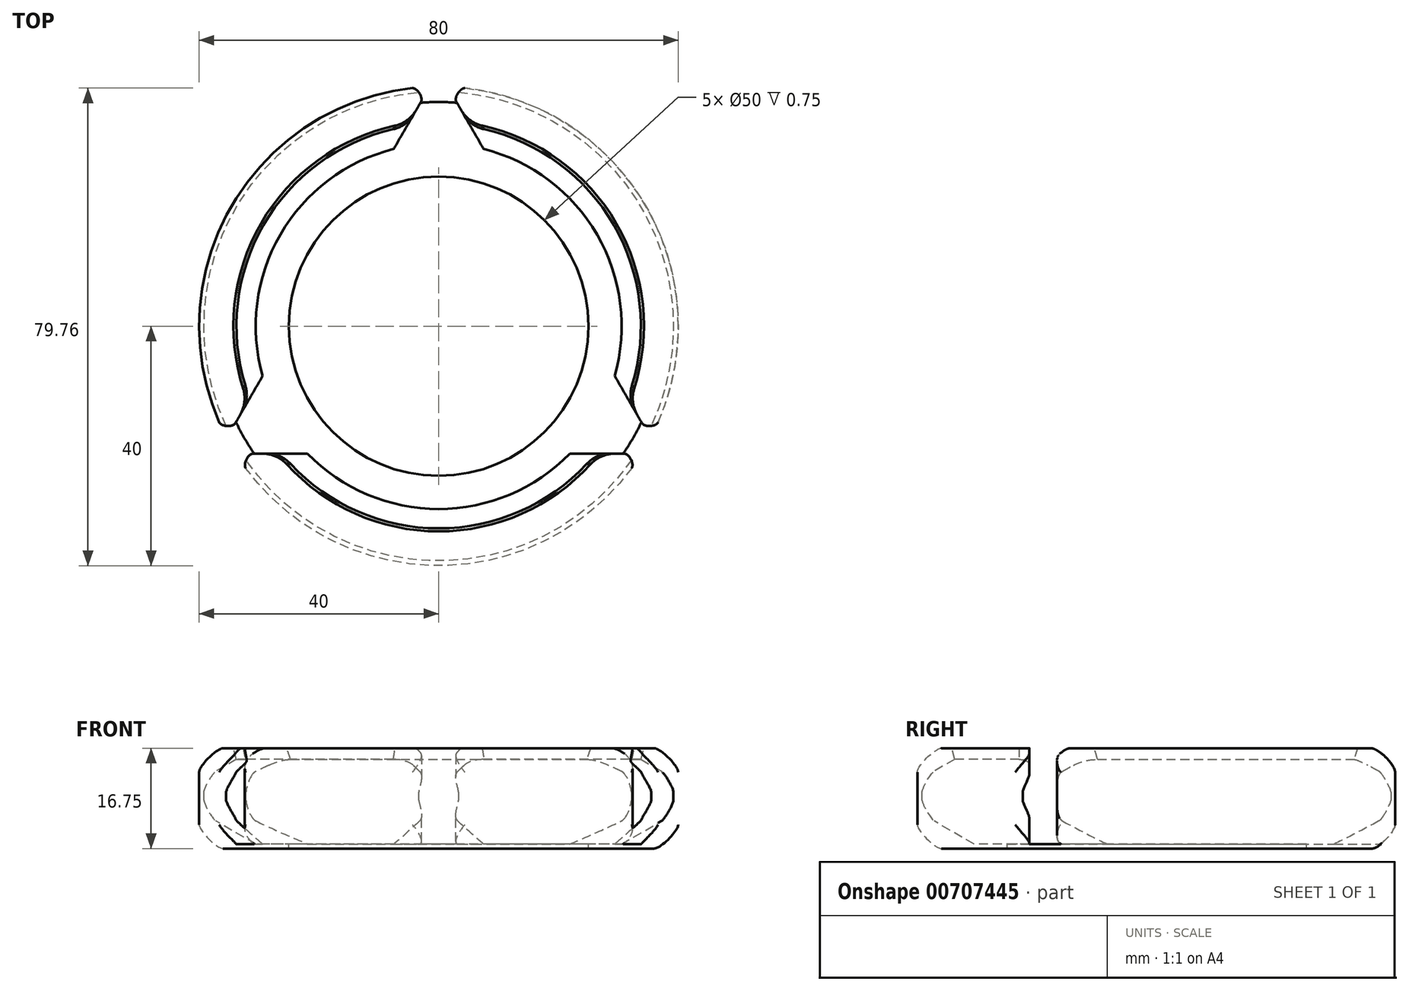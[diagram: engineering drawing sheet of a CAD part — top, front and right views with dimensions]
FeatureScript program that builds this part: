
annotation { "Feature Type Name" : "Feature", "Feature Type Description" : "" }
export const myFeature = defineFeature(function(context is Context, id is Id, definition is map)
    precondition{}
    {
        {
            var Q0;
            Q0=qCreatedBy(makeId("Right.planeOp"),FACE);
            var sketch = newSketch(context, id + "F0", { "sketchPlane" : qUnion([Q0])});
            skLineSegment(sketch, "E0", {"start": v(0, 0) * mm, "end": v(40, 0) * mm});
            skLineSegment(sketch, "E1", {"start": v(40, 0) * mm, "end": v(40, 16.75) * mm});
            skLineSegment(sketch, "E2", {"start": v(40, 16.75) * mm, "end": v(30.54, 16.75) * mm});
            skLineSegment(sketch, "E3", {"start": v(30.54, 16.75) * mm, "end": v(39.2, 11.75) * mm});
            skLineSegment(sketch, "E4", {"start": v(39.2, 11.75) * mm, "end": v(39.2, 5.75) * mm});
            skLineSegment(sketch, "E5", {"start": v(39.2, 5.75) * mm, "end": v(30.54, 0.75) * mm});
            skLineSegment(sketch, "E6", {"start": v(30.54, 0.75) * mm, "end": v(0, 0.75) * mm});
            skLineSegment(sketch, "E7", {"start": v(0, 0.75) * mm, "end": v(0, 0) * mm});
            skLineSegment(sketch, "E8", {"start": v(30.54, 0.75) * mm, "end": v(30.54, 16.75) * mm, "construction": true});
            skSolve(sketch);
        }
        {
            var Q0;
            Q0 = qSketchRegion(id + "F0", true);
            var Q1;
            Q1=sQuery(id+"F0.wireOp",EDGE,"E7");
            revolve(context, id + "F1", {"surfaceOperationType" : NewSurfaceOperationType.NEW, "entities" : qUnion([Q0]), "axis" : qUnion([Q1]), "revolveType" : RevolveType.FULL});
        }
        {
            var Q0;
            Q0=makeQuery(id+"F1.opRevolve","SWEPT_EDGE",EDGE,{"disambiguationData":[OSD([sQuery(id+"F0.wireOp",EDGE,"E0"),sQuery(id+"F0.wireOp",EDGE,"E1")])]});
            var Q1;
            Q1=makeQuery(id+"F1.opRevolve","SWEPT_EDGE",EDGE,{"disambiguationData":[OSD([sQuery(id+"F0.wireOp",EDGE,"E1"),sQuery(id+"F0.wireOp",EDGE,"E2")])]});
            var Q2;
            Q2=makeQuery(id+"F1.opRevolve","SWEPT_EDGE",EDGE,{"disambiguationData":[OSD([sQuery(id+"F0.wireOp",EDGE,"E4"),sQuery(id+"F0.wireOp",EDGE,"E5")])]});
            var Q3;
            Q3=makeQuery(id+"F1.opRevolve","SWEPT_FACE",FACE,{"disambiguationData":[OSD([sQuery(id+"F0.wireOp",EDGE,"E4")])]});
            fillet(context, id + "F2", {"entities" : qUnion([Q0, Q1, Q2, Q3]), "radius" : 4 * mm, "tangentPropagation" : true, "rho" : .2, "crossSection" : FilletCrossSection.CONIC, "allowEdgeOverflow" : false});
        }
        {
            var Q0;
            Q0=makeQuery(id+"F1.opRevolve","SWEPT_EDGE",EDGE,{"disambiguationData":[OSD([sQuery(id+"F0.wireOp",EDGE,"E2"),sQuery(id+"F0.wireOp",EDGE,"E3")])]});
            chamfer(context, id + "F3", {"entities" : qUnion([Q0]), "width" : 1 * mm, "tangentPropagation" : true});
        }
        {
            var Q0;
            Q0=makeQuery(id+"F1.opRevolve","SWEPT_FACE",FACE,{"disambiguationData":[OSD([sQuery(id+"F0.wireOp",EDGE,"E2")])]});
            var sketch = newSketch(context, id + "F4", { "sketchPlane" : qUnion([Q0])});
            skLineSegment(sketch, "E9", {"start": v(-1.5, 40) * mm, "end": v(1.5, 40) * mm});
            skLineSegment(sketch, "E10", {"start": v(1.5, 40) * mm, "end": v(35.4, -18.7) * mm});
            skLineSegment(sketch, "E11", {"start": v(35.4, -18.7) * mm, "end": v(33.9, -21.3) * mm});
            skLineSegment(sketch, "E12", {"start": v(33.9, -21.3) * mm, "end": v(-33.9, -21.3) * mm});
            skLineSegment(sketch, "E13", {"start": v(-33.9, -21.3) * mm, "end": v(-35.4, -18.7) * mm});
            skLineSegment(sketch, "E14", {"start": v(-35.4, -18.7) * mm, "end": v(-1.5, 40) * mm});
            skLineSegment(sketch, "E15", {"start": v(0, 40) * mm, "end": v(0, 0) * mm, "construction": true});
            skLineSegment(sketch, "E16", {"start": v(0, 0) * mm, "end": v(34.64, -20) * mm, "construction": true});
            skLineSegment(sketch, "E17", {"start": v(-34.64, -20) * mm, "end": v(0, 0) * mm, "construction": true});
            skSolve(sketch);
        }
        {
            var Q0;
            Q0 = qSketchRegion(id + "F4", true);
            var Q1;
            Q1=makeQuery(id+"F1.opRevolve","SWEPT_FACE",FACE,{"disambiguationData":[OSD([sQuery(id+"F0.wireOp",EDGE,"E6")])]});
            extrude(context, id + "F5", {"entities" : qUnion([Q0]), "operationType" : NewBodyOperationType.REMOVE, "endBound" : BoundingType.UP_TO_SURFACE, "oppositeDirection" : true, "depth" : 25 * mm, "endBoundEntityFace" : qUnion([Q1]), "offsetDistance" : 25 * mm});
        }
        {
            var Q0;
            Q0=makeQuery(id+"F5.boolean.opBoolean","INTERSECT",EDGE,{"disambiguationData":[OD(0.0)],"derivedFrom":[makeQuery(id+"F1.opRevolve","SWEPT_FACE",FACE,{"disambiguationData":[OSD([sQuery(id+"F0.wireOp",EDGE,"E1")])]}),makeQuery(id+"F5.opExtrude","SWEPT_FACE",FACE,{"disambiguationData":[OSD([sQuery(id+"F4.wireOp",EDGE,"E14")])]})]});
            var Q1;
            Q1=makeQuery(id+"F5.boolean.opBoolean","INTERSECT",EDGE,{"disambiguationData":[OD(0.0)],"derivedFrom":[makeQuery(id+"F1.opRevolve","SWEPT_FACE",FACE,{"disambiguationData":[OSD([sQuery(id+"F0.wireOp",EDGE,"E1")])]}),makeQuery(id+"F5.opExtrude","SWEPT_FACE",FACE,{"disambiguationData":[OSD([sQuery(id+"F4.wireOp",EDGE,"E12")])]})]});
            var Q2;
            Q2=makeQuery(id+"F5.boolean.opBoolean","INTERSECT",EDGE,{"disambiguationData":[OD(1.0)],"derivedFrom":[makeQuery(id+"F1.opRevolve","SWEPT_FACE",FACE,{"disambiguationData":[OSD([sQuery(id+"F0.wireOp",EDGE,"E1")])]}),makeQuery(id+"F5.opExtrude","SWEPT_FACE",FACE,{"disambiguationData":[OSD([sQuery(id+"F4.wireOp",EDGE,"E10")])]})]});
            var Q3;
            Q3=makeQuery(id+"F5.boolean.opBoolean","INTERSECT",EDGE,{"disambiguationData":[OD(1.0)],"derivedFrom":[makeQuery(id+"F1.opRevolve","SWEPT_FACE",FACE,{"disambiguationData":[OSD([sQuery(id+"F0.wireOp",EDGE,"E1")])]}),makeQuery(id+"F5.opExtrude","SWEPT_FACE",FACE,{"disambiguationData":[OSD([sQuery(id+"F4.wireOp",EDGE,"E12")])]})]});
            var Q4;
            Q4=makeQuery(id+"F5.boolean.opBoolean","INTERSECT",EDGE,{"disambiguationData":[OD(1.0)],"derivedFrom":[makeQuery(id+"F1.opRevolve","SWEPT_FACE",FACE,{"disambiguationData":[OSD([sQuery(id+"F0.wireOp",EDGE,"E1")])]}),makeQuery(id+"F5.opExtrude","SWEPT_FACE",FACE,{"disambiguationData":[OSD([sQuery(id+"F4.wireOp",EDGE,"E14")])]})]});
            var Q5;
            Q5=makeQuery(id+"F5.boolean.opBoolean","INTERSECT",EDGE,{"disambiguationData":[OD(0.0)],"derivedFrom":[makeQuery(id+"F1.opRevolve","SWEPT_FACE",FACE,{"disambiguationData":[OSD([sQuery(id+"F0.wireOp",EDGE,"E1")])]}),makeQuery(id+"F5.opExtrude","SWEPT_FACE",FACE,{"disambiguationData":[OSD([sQuery(id+"F4.wireOp",EDGE,"E10")])]})]});
            fillet(context, id + "F6", {"entities" : qUnion([Q0, Q1, Q2, Q3, Q4, Q5]), "radius" : 1.5 * mm, "rho" : .2, "crossSection" : FilletCrossSection.CONIC, "allowEdgeOverflow" : false});
        }
        {
            var Q0;
            Q0=makeQuery(id+"F5.boolean.opBoolean","INTERSECT",EDGE,{"disambiguationData":[OD(1.0)],"derivedFrom":[makeQuery(id+"F3.opChamfer","BLEND_FACE",FACE,{"disambiguationData":[OSD([sQuery(id+"F0.wireOp",EDGE,"E2"),sQuery(id+"F0.wireOp",EDGE,"E3")])]}),makeQuery(id+"F5.opExtrude","SWEPT_FACE",FACE,{"disambiguationData":[OSD([sQuery(id+"F4.wireOp",EDGE,"E14")])]})]});
            var Q1;
            Q1=makeQuery(id+"F5.boolean.opBoolean","INTERSECT",EDGE,{"disambiguationData":[OD(0.0)],"derivedFrom":[makeQuery(id+"F3.opChamfer","BLEND_FACE",FACE,{"disambiguationData":[OSD([sQuery(id+"F0.wireOp",EDGE,"E2"),sQuery(id+"F0.wireOp",EDGE,"E3")])]}),makeQuery(id+"F5.opExtrude","SWEPT_FACE",FACE,{"disambiguationData":[OSD([sQuery(id+"F4.wireOp",EDGE,"E10")])]})]});
            var Q2;
            Q2=makeQuery(id+"F5.boolean.opBoolean","INTERSECT",EDGE,{"disambiguationData":[OD(1.0)],"derivedFrom":[makeQuery(id+"F3.opChamfer","BLEND_FACE",FACE,{"disambiguationData":[OSD([sQuery(id+"F0.wireOp",EDGE,"E2"),sQuery(id+"F0.wireOp",EDGE,"E3")])]}),makeQuery(id+"F5.opExtrude","SWEPT_FACE",FACE,{"disambiguationData":[OSD([sQuery(id+"F4.wireOp",EDGE,"E10")])]})]});
            var Q3;
            Q3=makeQuery(id+"F5.boolean.opBoolean","INTERSECT",EDGE,{"disambiguationData":[OD(1.0)],"derivedFrom":[makeQuery(id+"F3.opChamfer","BLEND_FACE",FACE,{"disambiguationData":[OSD([sQuery(id+"F0.wireOp",EDGE,"E2"),sQuery(id+"F0.wireOp",EDGE,"E3")])]}),makeQuery(id+"F5.opExtrude","SWEPT_FACE",FACE,{"disambiguationData":[OSD([sQuery(id+"F4.wireOp",EDGE,"E12")])]})]});
            var Q4;
            Q4=makeQuery(id+"F5.boolean.opBoolean","INTERSECT",EDGE,{"disambiguationData":[OD(0.0)],"derivedFrom":[makeQuery(id+"F3.opChamfer","BLEND_FACE",FACE,{"disambiguationData":[OSD([sQuery(id+"F0.wireOp",EDGE,"E2"),sQuery(id+"F0.wireOp",EDGE,"E3")])]}),makeQuery(id+"F5.opExtrude","SWEPT_FACE",FACE,{"disambiguationData":[OSD([sQuery(id+"F4.wireOp",EDGE,"E12")])]})]});
            var Q5;
            Q5=makeQuery(id+"F5.boolean.opBoolean","INTERSECT",EDGE,{"disambiguationData":[OD(0.0)],"derivedFrom":[makeQuery(id+"F3.opChamfer","BLEND_FACE",FACE,{"disambiguationData":[OSD([sQuery(id+"F0.wireOp",EDGE,"E2"),sQuery(id+"F0.wireOp",EDGE,"E3")])]}),makeQuery(id+"F5.opExtrude","SWEPT_FACE",FACE,{"disambiguationData":[OSD([sQuery(id+"F4.wireOp",EDGE,"E14")])]})]});
            fillet(context, id + "F7", {"entities" : qUnion([Q0, Q1, Q2, Q3, Q4, Q5]), "radius" : 5 * mm, "tangentPropagation" : true, "allowEdgeOverflow" : false});
        }
        {
            var Q0;
            Q0=makeQuery(id+"FrtOHLsR6oiIfuC_1.boolean.opBoolean","MERGE",FACE,{"derivedFrom":[makeQuery(id+"F1.opRevolve","SWEPT_FACE",FACE,{"disambiguationData":[OSD([sQuery(id+"F0.wireOp",EDGE,"E6")])]}),makeQuery(id+"FrtOHLsR6oiIfuC_1.opExtrude","CAP_FACE",FACE,{"disambiguationData":[OSD([sQuery(id+"FDtI83EdFGZSK6q_1.wireOp",EDGE,"AMy5WTtV-pqfj-7Uts-uxfa-YCOQgYczJXpA.bottom"),sQuery(id+"FDtI83EdFGZSK6q_1.wireOp",EDGE,"AMy5WTtV-pqfj-7Uts-uxfa-YCOQgYczJXpA.top"),sQuery(id+"FDtI83EdFGZSK6q_1.wireOp",EDGE,"AMy5WTtV-pqfj-7Uts-uxfa-YCOQgYczJXpA.left"),sQuery(id+"FDtI83EdFGZSK6q_1.wireOp",EDGE,"AMy5WTtV-pqfj-7Uts-uxfa-YCOQgYczJXpA.right")])],"isStart":true})]});
            var sketch = newSketch(context, id + "F8", { "sketchPlane" : qUnion([Q0])});
            skCircle(sketch, "E18", {"center": v(0, 0) * mm, "radius": 25 * mm});
            skSolve(sketch);
        }
        {
            var Q0;
            Q0 = qSketchRegion(id + "F8", true);
            var Q1;
            Q1=sQuery(id+"F8.wireOp",EDGE,"E18");
            extrude(context, id + "F9", {"entities" : qUnion([Q0]), "operationType" : NewBodyOperationType.REMOVE, "surfaceEntities" : qUnion([Q1]), "endBound" : BoundingType.UP_TO_NEXT, "oppositeDirection" : true, "depth" : 25 * mm, "offsetDistance" : 25 * mm});
        }
    });
